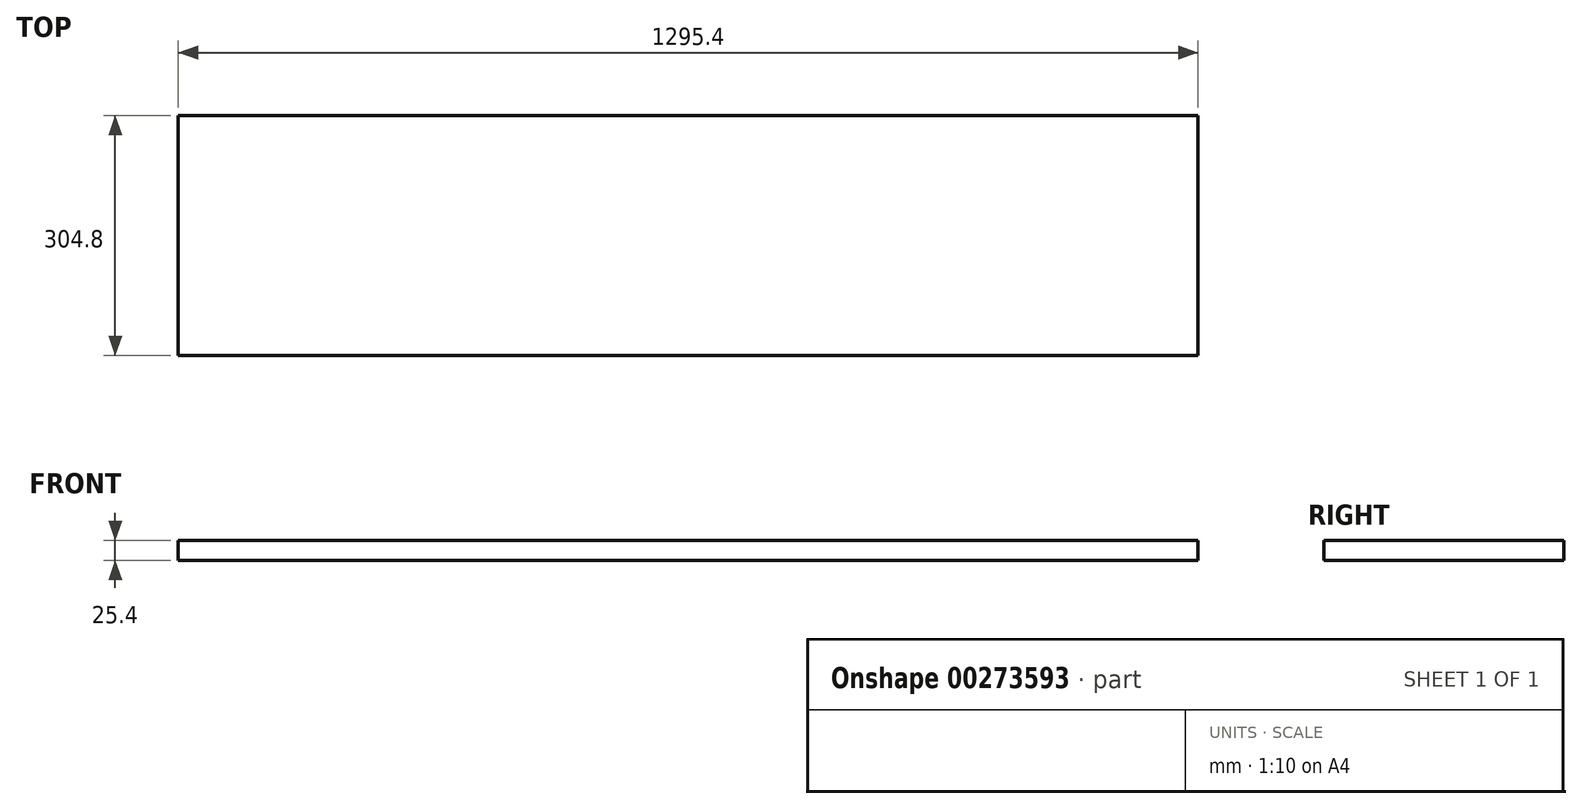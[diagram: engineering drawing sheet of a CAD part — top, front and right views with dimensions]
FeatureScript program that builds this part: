
annotation { "Feature Type Name" : "Feature", "Feature Type Description" : "" }
export const myFeature = defineFeature(function(context is Context, id is Id, definition is map)
    precondition{}
    {
        {
            var Q0;
            Q0=qCreatedBy(makeId("Top.planeOp"),FACE);
            var sketch = newSketch(context, id + "F0", { "sketchPlane" : qUnion([Q0])});
            skLineSegment(sketch, "E0.bottom", {"start": v(-43.97, 292.26) * mm, "end": v(1251.43, 292.26) * mm});
            skLineSegment(sketch, "E0.top", {"start": v(-43.97, -12.54) * mm, "end": v(1251.43, -12.54) * mm});
            skLineSegment(sketch, "E0.left", {"start": v(-43.97, 292.26) * mm, "end": v(-43.97, -12.54) * mm});
            skLineSegment(sketch, "E0.right", {"start": v(1251.43, 292.26) * mm, "end": v(1251.43, -12.54) * mm});
            skSolve(sketch);
        }
        {
            var Q0;
            Q0 = qSketchRegion(id + "F0", true);
            extrude(context, id + "F1", {"entities" : qUnion([Q0]), "oppositeDirection" : true, "depth" : 25.4 * mm});
        }
    });
